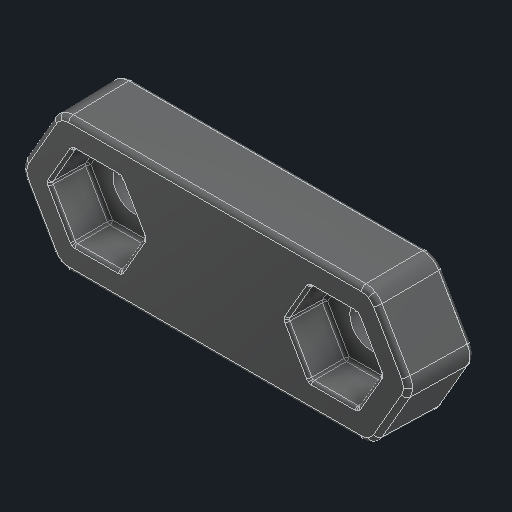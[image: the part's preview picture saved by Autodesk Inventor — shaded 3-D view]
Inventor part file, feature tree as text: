
AUTODESK INVENTOR PART (.ipt)
format: ipt  version: 2024 (Build 280153000, 153)  size: 370,688 bytes
history: native  units: in
note: dims shown in document units (in); Inventor stores cm internally (conversion verified against a paired STEP export)
features: fillet x1
ambient origin geometry x8: Origin, YZ Plane, XZ Plane, XY Plane, X Axis, Y Axis, Z Axis, Center Point
bodies: Solid1 (feature_tree)
feature tree (1):
  fillet  "Fillet8"  [1 undecoded]
note: 1 required parameter value undecoded (feature->parameter linkage not recoverable at this tier; creation-order binding heuristic only, values carry confidence <= 0.55)
